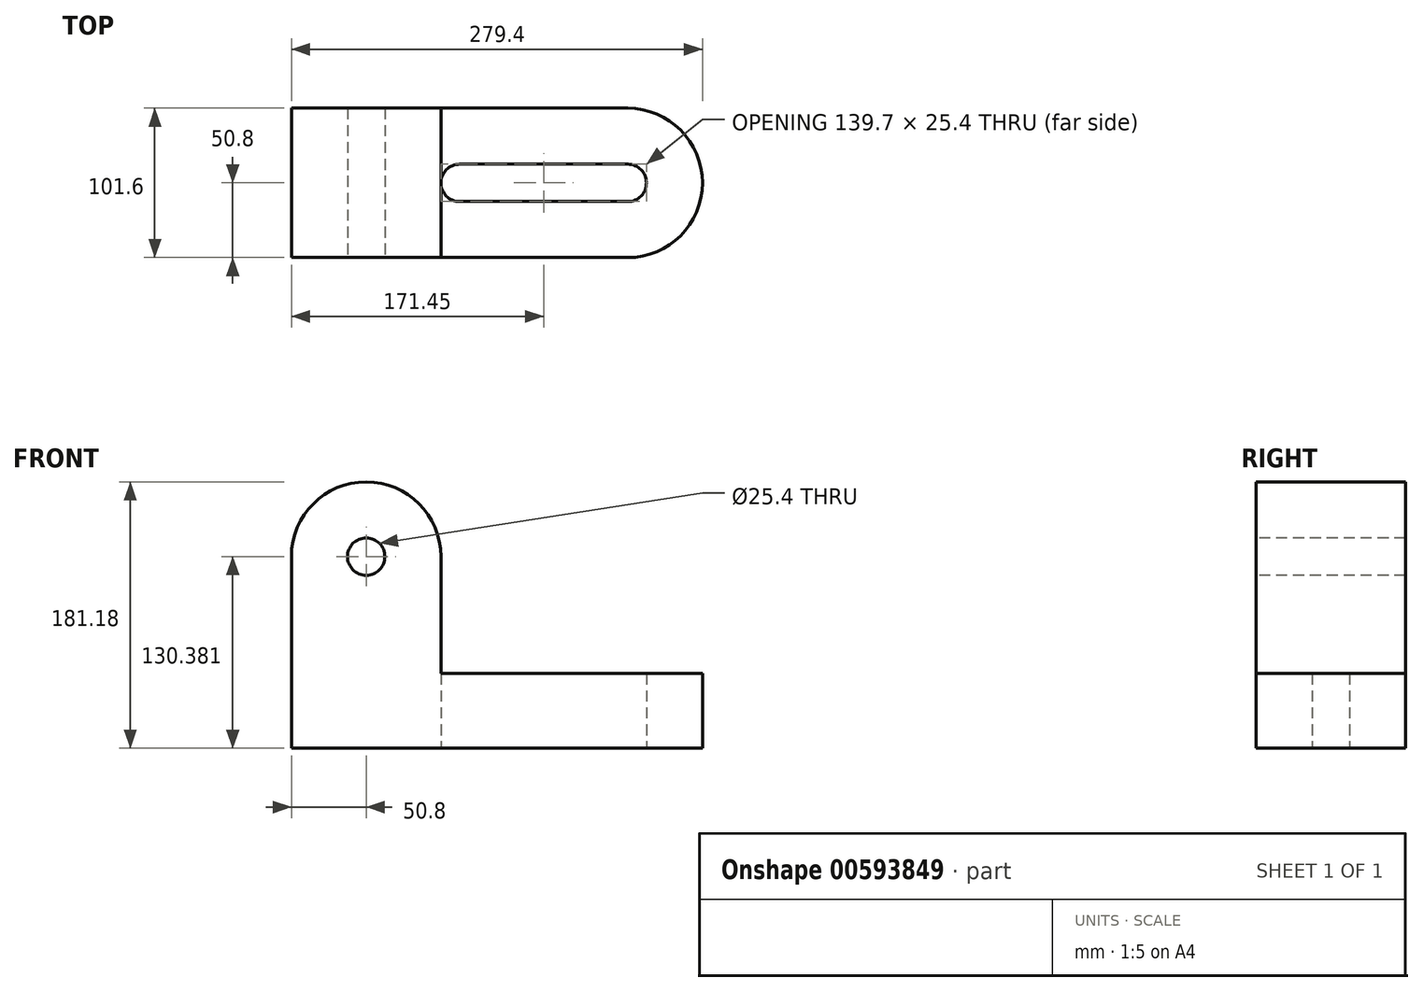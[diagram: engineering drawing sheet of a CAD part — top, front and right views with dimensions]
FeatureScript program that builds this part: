
annotation { "Feature Type Name" : "Feature", "Feature Type Description" : "" }
export const myFeature = defineFeature(function(context is Context, id is Id, definition is map)
    precondition{}
    {
        {
            var Q0;
            Q0=qCreatedBy(makeId("Top.planeOp"),FACE);
            var sketch = newSketch(context, id + "F0", { "sketchPlane" : qUnion([Q0])});
            skLineSegment(sketch, "E0.bottom", {"start": v(114.3, 50.8) * mm, "end": v(-114.3, 50.8) * mm});
            skLineSegment(sketch, "E0.top", {"start": v(114.3, -50.8) * mm, "end": v(-114.3, -50.8) * mm});
            skLineSegment(sketch, "E0.right", {"start": v(-114.3, 50.8) * mm, "end": v(-114.3, -50.8) * mm});
            skArc(sketch, "E1", {"start": v(114.3, -50.8) * mm, "mid": v(165.1, 0) * mm, "end": v(114.3, 50.8) * mm});
            skArc(sketch, "E2.0.startCap", {"start": v(0, -12.7) * mm, "mid": v(-12.7, 0) * mm, "end": v(0, 12.7) * mm});
            skArc(sketch, "E2.0.endCap", {"start": v(114.3, 12.7) * mm, "mid": v(127, 0) * mm, "end": v(114.3, -12.7) * mm});
            skLineSegment(sketch, "E2.0.left", {"start": v(0, 12.7) * mm, "end": v(114.3, 12.7) * mm});
            skLineSegment(sketch, "E2.0.right", {"start": v(0, -12.7) * mm, "end": v(114.3, -12.7) * mm});
            skSolve(sketch);
        }
        {
            var Q0;
            Q0 = qSketchRegion(id + "F0", true);
            extrude(context, id + "F1", {"entities" : qUnion([Q0]), "depth" : 50.8 * mm, "offsetDistance" : 25.4 * mm});
        }
        {
            var Q0;
            Q0=makeQuery(id+"F1.opExtrude","SWEPT_FACE",FACE,{"disambiguationData":[OSD([sQuery(id+"F0.wireOp",EDGE,"E0.top")])]});
            var sketch = newSketch(context, id + "F2", { "sketchPlane" : qUnion([Q0])});
            skLineSegment(sketch, "E3.0", {"start": v(114.3, 50.8) * mm, "end": v(-114.3, 50.8) * mm});
            skLineSegment(sketch, "E4", {"start": v(-114.3, 50.8) * mm, "end": v(-114.3, 130.38) * mm});
            skLineSegment(sketch, "E5", {"start": v(-12.7, 130.38) * mm, "end": v(-12.7, 50.8) * mm});
            skArc(sketch, "E6", {"start": v(-114.3, 130.38) * mm, "mid": v(-63.5, 181.18) * mm, "end": v(-12.7, 130.38) * mm});
            skCircle(sketch, "E7", {"center": v(-63.5, 130.38) * mm, "radius": 12.7 * mm});
            skSolve(sketch);
        }
        {
            var Q0;
            Q0 = qSketchRegion(id + "F2", true);
            extrude(context, id + "F3", {"entities" : qUnion([Q0]), "operationType" : NewBodyOperationType.ADD, "oppositeDirection" : true, "depth" : 101.6 * mm, "offsetDistance" : 25.4 * mm});
        }
    });
